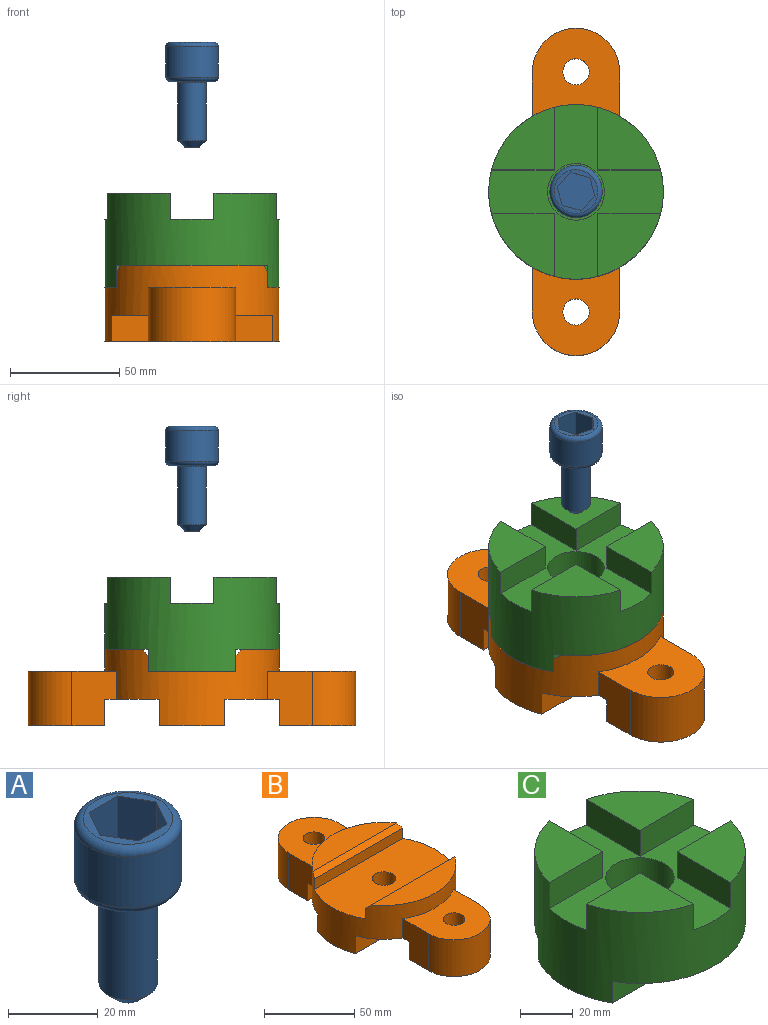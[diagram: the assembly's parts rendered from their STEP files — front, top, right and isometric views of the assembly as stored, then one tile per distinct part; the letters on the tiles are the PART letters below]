
ASSEMBLY  parts=3 mates=2
PART A: 16 faces, bbox 26x26x48 mm
  f0: plane 20x20mm, normal (0,0,1), area 103.7mm2, adj f5,f6,f7,f8,f9,f10,f13
  f1: cylinder r=12mm len=24mm, axis (0,0,-1), area 1055.6mm2, adj f12,f13
  f2: plane 20x20mm, normal (0,0,-1), area 160.2mm2, adj f12,f14
  f3: cylinder r=6.5mm len=26.5mm, axis (0,0,1), area 1082.3mm2, adj f14,f15
  f4: plane 7x7mm, normal (0,0,-1), area 38.5mm2, adj f15
  f5: plane 13x9mm, normal (0,1,0), area 117mm2, adj f0,f6,f10,f11
  f6: plane 13x7.79mm, normal (-0.87,0.5,0), area 117mm2, adj f0,f5,f7,f11
  f7: plane 13x7.79mm, normal (-0.87,-0.5,0), area 117mm2, adj f0,f6,f8,f11
  f8: plane 13x9mm, normal (0,-1,0), area 117mm2, adj f0,f7,f9,f11
  f9: plane 13x7.79mm, normal (0.87,-0.5,0), area 117mm2, adj f0,f8,f10,f11
  f10: plane 13x7.79mm, normal (0.87,0.5,0), area 117mm2, adj f0,f5,f9,f11
  f11: plane 18x15.59mm, normal (0,0,1), area 210.4mm2, adj f5,f6,f7,f8,f9,f10
  f12: torus R=10mm, axis (0,0,1), area 222.5mm2, adj f1,f2
  f13: torus R=10mm, axis (0,0,1), area 222.5mm2, adj f0,f1
  f14: torus R=7mm, axis (0,0,1), area 33mm2, adj f2,f3
  f15: cone r=6.5mm half-angle=45deg, axis (0,0,1), area 133.3mm2, adj f3,f4
PART B: 28 faces, bbox 80x150x35 mm
  f0: plane 25x20.36mm, normal (1,0,0), area 444.7mm2, adj f4,f9,f10,f15,f20,f22
  f1: plane 25x20.36mm, normal (-1,0,0), area 444.7mm2, adj f4,f9,f10,f15,f20,f22
  f2: plane 25x20.36mm, normal (-1,0,0), area 444.7mm2, adj f4,f5,f7,f11,f23,f25
  f3: plane 25x20.36mm, normal (1,0,0), area 444.7mm2, adj f4,f5,f7,f11,f23,f25
  f4: cylinder r=40mm len=80mm, axis (0,0,-1), area 4570.6mm2, adj f0,f1,f2,f3,f6,f7,f8,f9
  f5: plane 40x35mm, normal (0,0,-1), area 1115.2mm2, adj f2,f3,f11,f14,f23
  f6: plane 80x30mm, normal (0,0,-1), area 2209.8mm2, adj f4,f13,f21,f24
  f7: plane 40.36x40mm, normal (0,0,1), area 1184.6mm2, adj f2,f3,f4,f11,f14
  f8: plane 80x40mm, normal (0,0,1), area 2928.4mm2, adj f4,f13,f16,f18
  f9: plane 40.36x40mm, normal (0,0,1), area 1184.6mm2, adj f0,f1,f4,f10,f12
  f10: cylinder r=20mm len=40mm, axis (0,0,-1), area 1570.8mm2, adj f0,f1,f9,f15
  f11: cylinder r=20mm len=40mm, axis (0,0,-1), area 1570.8mm2, adj f2,f3,f5,f7
  f12: cylinder r=6mm len=25mm, axis (0,0,-1), area 942.5mm2, adj f9,f15
  f13: cylinder r=6.5mm len=25mm, axis (0,0,-1), area 1021mm2, adj f6,f8
  f14: cylinder r=6mm len=25mm, axis (0,0,-1), area 942.5mm2, adj f5,f7
  f15: plane 40x35mm, normal (0,0,-1), area 1115.2mm2, adj f0,f1,f10,f12,f20
  f16: plane 69.28x7mm, normal (0,-1,0), area 485mm2, adj f4,f8,f27
  f17: plane 65.45x17mm, normal (0,0,1), area 780.4mm2, adj f4,f27
  f18: plane 69.28x7mm, normal (0,1,0), area 485mm2, adj f4,f8,f26
  f19: plane 65.45x17mm, normal (0,0,1), area 780.4mm2, adj f4,f26
  f20: plane 40x12mm, normal (0,-1,0), area 480mm2, adj f0,f1,f15,f22
  f21: plane 74.16x12mm, normal (0,1,0), area 889.9mm2, adj f4,f6,f22
  f22: plane 74.16x25mm, normal (0,0,-1), area 1411.4mm2, adj f0,f1,f4,f20,f21
  f23: plane 40x12mm, normal (0,1,0), area 480mm2, adj f2,f3,f5,f25
  f24: plane 74.16x12mm, normal (0,-1,0), area 889.9mm2, adj f4,f6,f25
  f25: plane 74.16x25mm, normal (0,0,-1), area 1411.4mm2, adj f2,f3,f4,f23,f24
  f26: plane 69.28x3mm, normal (0,0.71,0.71), area 286.1mm2, adj f4,f18,f19
  f27: plane 69.28x3mm, normal (0,-0.71,0.71), area 286.1mm2, adj f4,f16,f17
PART C: 22 faces, bbox 80x80x43 mm
  f0: plane 28.73x28.73mm, normal (0,0,1), area 565.1mm2, adj f5,f12,f13
  f1: plane 28.73x28.73mm, normal (0,0,1), area 565.1mm2, adj f5,f16,f17
  f2: plane 28.73x28.73mm, normal (0,0,1), area 565.1mm2, adj f5,f11,f18
  f3: plane 69.28x10mm, normal (0,-1,0), area 692.8mm2, adj f5,f7,f8
  f4: plane 69.28x10mm, normal (0,1,0), area 692.8mm2, adj f5,f7,f10
  f5: cylinder r=40mm len=80mm, axis (0,0,-1), area 8161.3mm2, adj f0,f1,f2,f3,f4,f7,f8,f9
  f6: cylinder r=6.5mm len=13mm, axis (0,0,-1), area 530.9mm2, adj f7,f20
  f7: plane 80x40mm, normal (0,0,-1), area 2928.4mm2, adj f3,f4,f5,f6
  f8: plane 69.28x20mm, normal (0,0,-1), area 982.7mm2, adj f3,f5
  f9: plane 28.73x28.73mm, normal (0,0,1), area 565.1mm2, adj f5,f14,f15
  f10: plane 69.28x20mm, normal (0,0,-1), area 982.7mm2, adj f4,f5
  f11: plane 28.73x12mm, normal (0,1,0), area 344.8mm2, adj f2,f5,f18,f19
  f12: plane 28.73x12mm, normal (0,-1,0), area 344.8mm2, adj f0,f5,f13,f19
  f13: plane 28.73x12mm, normal (-1,0,0), area 344.8mm2, adj f0,f5,f12,f19
  f14: plane 28.73x12mm, normal (1,0,0), area 344.8mm2, adj f5,f9,f15,f19
  f15: plane 28.73x12mm, normal (0,-1,0), area 344.8mm2, adj f5,f9,f14,f19
  f16: plane 28.73x12mm, normal (0,1,0), area 344.8mm2, adj f1,f5,f17,f19
  f17: plane 28.73x12mm, normal (1,0,0), area 344.8mm2, adj f1,f5,f16,f19
  f18: plane 28.73x12mm, normal (-1,0,0), area 344.8mm2, adj f2,f5,f11,f19
  f19: plane 80x80mm, normal (0,0,1), area 2235.4mm2, adj f5,f11,f12,f13,f14,f15,f16,f17
  f20: plane 26x26mm, normal (0,0,1), area 398.2mm2, adj f6,f21
  f21: cylinder r=13mm len=26mm, axis (0,0,1), area 1470.3mm2, adj f19,f20
PLACE A rot(axis=(0,0,1),45.2deg) t=(0,0,81.15)mm
PLACE B at identity fixed
PLACE C at identity
MATE cylindrical A.f3 <-> C.f21  axis (0,0,1) through (0,0,118.65)mm
MATE fastened C.f6 <-> B.f13  axis (0,0,1) through (0,0,25)mm
